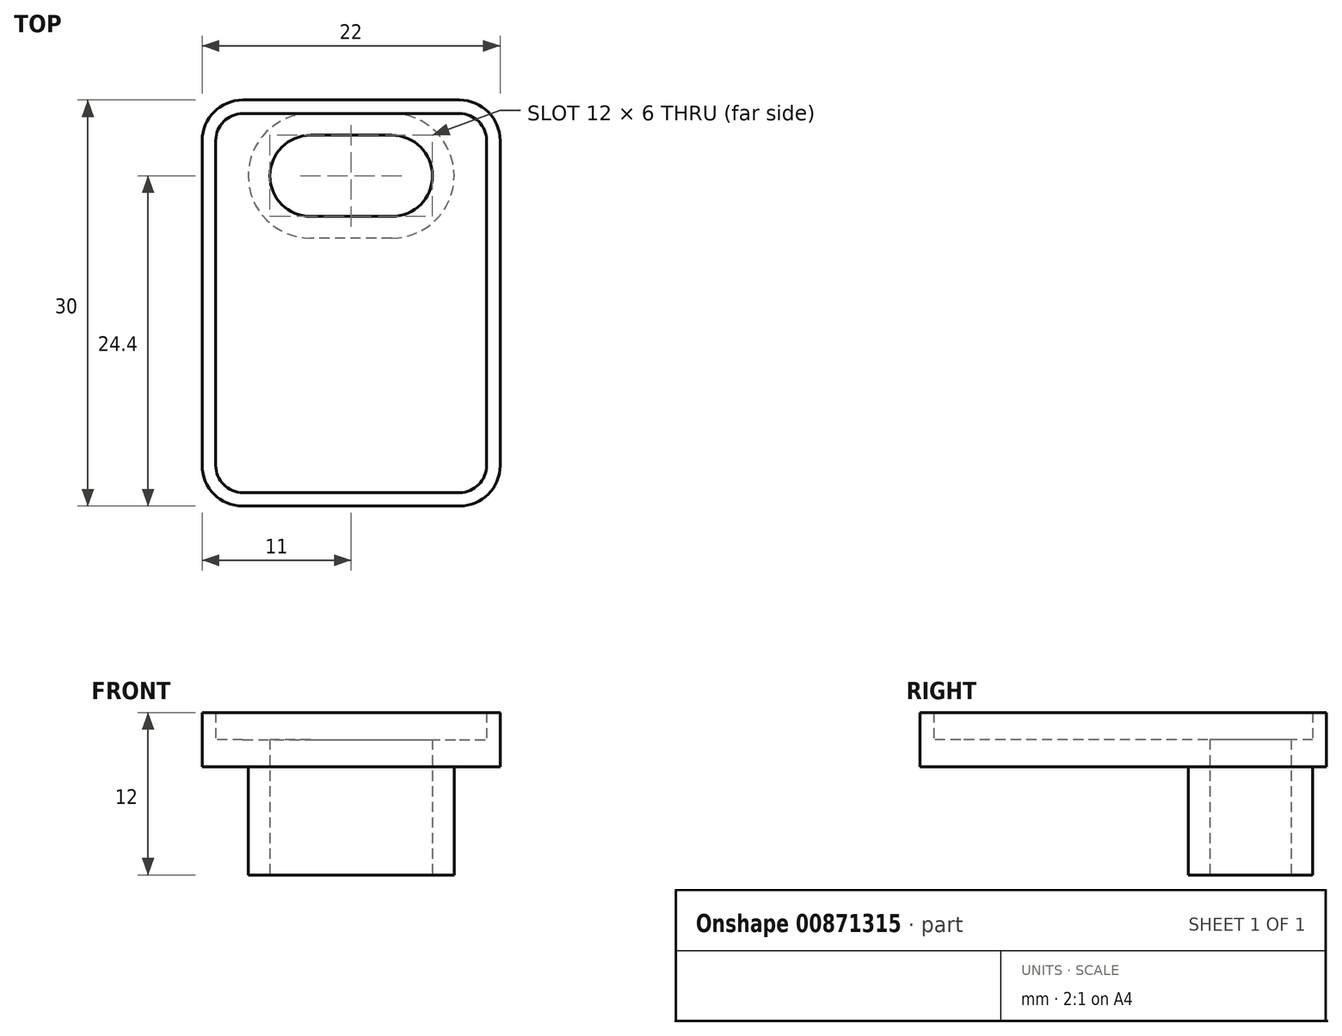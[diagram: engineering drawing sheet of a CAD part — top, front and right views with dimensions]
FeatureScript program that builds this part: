
annotation { "Feature Type Name" : "Feature", "Feature Type Description" : "" }
export const myFeature = defineFeature(function(context is Context, id is Id, definition is map)
    precondition{}
    {
        {
            var Q0;
            Q0=qCreatedBy(makeId("Top.planeOp"),FACE);
            var sketch = newSketch(context, id + "F0", { "sketchPlane" : qUnion([Q0])});
            skArc(sketch, "E0", {"start": v(-3, 3) * mm, "mid": v(-6, 0) * mm, "end": v(-3, -3) * mm});
            skArc(sketch, "E1", {"start": v(3, -3) * mm, "mid": v(6, 0) * mm, "end": v(3, 3) * mm});
            skLineSegment(sketch, "E2", {"start": v(-3, 3) * mm, "end": v(3, 3) * mm});
            skLineSegment(sketch, "E3", {"start": v(3, -3) * mm, "end": v(-3, -3) * mm});
            skArc(sketch, "E4.0", {"start": v(3, -4.6) * mm, "mid": v(7.6, 0) * mm, "end": v(3, 4.6) * mm});
            skLineSegment(sketch, "E4.1", {"start": v(3, -4.6) * mm, "end": v(-3, -4.6) * mm});
            skArc(sketch, "E4.2", {"start": v(-3, 4.6) * mm, "mid": v(-7.6, 0) * mm, "end": v(-3, -4.6) * mm});
            skLineSegment(sketch, "E4.3", {"start": v(-3, 4.6) * mm, "end": v(3, 4.6) * mm});
            skSolve(sketch);
        }
        {
            var Q0;
            Q0 = qSketchRegion(id + "F0", true);
            extrude(context, id + "F1", {"entities" : qUnion([Q0]), "depth" : 8 * mm, "offsetDistance" : 25.4 * mm});
        }
        {
            var Q0;
            Q0=makeQuery(id+"F1.opExtrude","CAP_FACE",FACE,{"disambiguationData":[OSD([sQuery(id+"F0.wireOp",EDGE,"E0"),sQuery(id+"F0.wireOp",EDGE,"E1"),sQuery(id+"F0.wireOp",EDGE,"E2"),sQuery(id+"F0.wireOp",EDGE,"E3"),sQuery(id+"F0.wireOp",EDGE,"E4.0"),sQuery(id+"F0.wireOp",EDGE,"E4.1"),sQuery(id+"F0.wireOp",EDGE,"E4.2"),sQuery(id+"F0.wireOp",EDGE,"E4.3")])],"isStart":false});
            var sketch = newSketch(context, id + "F2", { "sketchPlane" : qUnion([Q0])});
            skLineSegment(sketch, "E5", {"start": v(-8, 5.6) * mm, "end": v(8, 5.6) * mm});
            skLineSegment(sketch, "E6", {"start": v(-11, 2.6) * mm, "end": v(-11, -21.4) * mm});
            skLineSegment(sketch, "E7", {"start": v(-8, -24.4) * mm, "end": v(8, -24.4) * mm});
            skLineSegment(sketch, "E8", {"start": v(11, -21.4) * mm, "end": v(11, 2.6) * mm});
            skPoint(sketch, "E9.visualSharp", {"position": v(-11, 5.6) * mm});
            skArc(sketch, "E9.filletArc", {"start": v(-8, 5.6) * mm, "mid": v(-10.12, 4.72) * mm, "end": v(-11, 2.6) * mm});
            skPoint(sketch, "E10.visualSharp", {"position": v(11, 5.6) * mm});
            skArc(sketch, "E10.filletArc", {"start": v(11, 2.6) * mm, "mid": v(10.12, 4.72) * mm, "end": v(8, 5.6) * mm});
            skPoint(sketch, "E11.visualSharp", {"position": v(11, -24.4) * mm});
            skArc(sketch, "E11.filletArc", {"start": v(8, -24.4) * mm, "mid": v(10.12, -23.52) * mm, "end": v(11, -21.4) * mm});
            skPoint(sketch, "E12.visualSharp", {"position": v(-11, -24.4) * mm});
            skArc(sketch, "E12.filletArc", {"start": v(-11, -21.4) * mm, "mid": v(-10.12, -23.52) * mm, "end": v(-8, -24.4) * mm});
            skArc(sketch, "E13.0", {"start": v(3, -3) * mm, "mid": v(6, 0) * mm, "end": v(3, 3) * mm});
            skLineSegment(sketch, "E13.1", {"start": v(3, -3) * mm, "end": v(-3, -3) * mm});
            skArc(sketch, "E13.2", {"start": v(-3, 3) * mm, "mid": v(-6, 0) * mm, "end": v(-3, -3) * mm});
            skLineSegment(sketch, "E13.3", {"start": v(-3, 3) * mm, "end": v(3, 3) * mm});
            skSolve(sketch);
        }
        {
            var Q0;
            Q0 = qSketchRegion(id + "F2", true);
            extrude(context, id + "F3", {"entities" : qUnion([Q0]), "operationType" : NewBodyOperationType.ADD, "depth" : 2 * mm, "offsetDistance" : 25 * mm});
        }
        {
            var Q0;
            Q0=makeQuery(id+"F3.opExtrude","CAP_FACE",FACE,{"disambiguationData":[OSD([sQuery(id+"F2.wireOp",EDGE,"E5"),sQuery(id+"F2.wireOp",EDGE,"E6"),sQuery(id+"F2.wireOp",EDGE,"E7"),sQuery(id+"F2.wireOp",EDGE,"E8"),sQuery(id+"F2.wireOp",EDGE,"E9.filletArc"),sQuery(id+"F2.wireOp",EDGE,"E10.filletArc"),sQuery(id+"F2.wireOp",EDGE,"E11.filletArc"),sQuery(id+"F2.wireOp",EDGE,"E12.filletArc"),sQuery(id+"F2.wireOp",EDGE,"E13.0"),sQuery(id+"F2.wireOp",EDGE,"E13.1"),sQuery(id+"F2.wireOp",EDGE,"E13.2"),sQuery(id+"F2.wireOp",EDGE,"E13.3")])],"isStart":false});
            var sketch = newSketch(context, id + "F4", { "sketchPlane" : qUnion([Q0])});
            skLineSegment(sketch, "E14.0", {"start": v(10, -21.4) * mm, "end": v(10, 2.6) * mm});
            skLineSegment(sketch, "E14.1", {"start": v(-8, -23.4) * mm, "end": v(8, -23.4) * mm});
            skLineSegment(sketch, "E14.2", {"start": v(-10, 2.6) * mm, "end": v(-10, -21.4) * mm});
            skLineSegment(sketch, "E14.3", {"start": v(-8, 4.6) * mm, "end": v(8, 4.6) * mm});
            skPoint(sketch, "E15.visualSharp", {"position": v(10, 4.6) * mm});
            skArc(sketch, "E15.filletArc", {"start": v(10, 2.6) * mm, "mid": v(9.41, 4.01) * mm, "end": v(8, 4.6) * mm});
            skPoint(sketch, "E16.visualSharp", {"position": v(-10, 4.6) * mm});
            skArc(sketch, "E16.filletArc", {"start": v(-8, 4.6) * mm, "mid": v(-9.41, 4.01) * mm, "end": v(-10, 2.6) * mm});
            skPoint(sketch, "E17.visualSharp", {"position": v(-10, -23.4) * mm});
            skArc(sketch, "E17.filletArc", {"start": v(-10, -21.4) * mm, "mid": v(-9.41, -22.81) * mm, "end": v(-8, -23.4) * mm});
            skPoint(sketch, "E18.visualSharp", {"position": v(10, -23.4) * mm});
            skArc(sketch, "E18.filletArc", {"start": v(8, -23.4) * mm, "mid": v(9.41, -22.81) * mm, "end": v(10, -21.4) * mm});
            skArc(sketch, "E19.0", {"start": v(-8, 5.6) * mm, "mid": v(-10.12, 4.72) * mm, "end": v(-11, 2.6) * mm});
            skLineSegment(sketch, "E19.1", {"start": v(-11, 2.6) * mm, "end": v(-11, -21.4) * mm});
            skLineSegment(sketch, "E19.2", {"start": v(-8, 5.6) * mm, "end": v(8, 5.6) * mm});
            skArc(sketch, "E19.3", {"start": v(-11, -21.4) * mm, "mid": v(-10.12, -23.52) * mm, "end": v(-8, -24.4) * mm});
            skArc(sketch, "E19.4", {"start": v(11, 2.6) * mm, "mid": v(10.12, 4.72) * mm, "end": v(8, 5.6) * mm});
            skLineSegment(sketch, "E19.5", {"start": v(11, -21.4) * mm, "end": v(11, 2.6) * mm});
            skArc(sketch, "E19.6", {"start": v(8, -24.4) * mm, "mid": v(10.12, -23.52) * mm, "end": v(11, -21.4) * mm});
            skLineSegment(sketch, "E19.7", {"start": v(-8, -24.4) * mm, "end": v(8, -24.4) * mm});
            skSolve(sketch);
        }
        {
            var Q0;
            Q0 = qSketchRegion(id + "F4", true);
            extrude(context, id + "F5", {"entities" : qUnion([Q0]), "operationType" : NewBodyOperationType.ADD, "depth" : 2 * mm, "offsetDistance" : 25 * mm});
        }
    });
